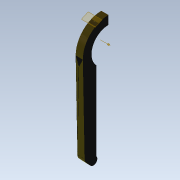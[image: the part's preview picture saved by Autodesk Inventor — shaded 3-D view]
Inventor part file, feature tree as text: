
AUTODESK INVENTOR PART (.ipt)
format: ipt  version: 2021 (Build 250183000, 183)  size: 1,088,512 bytes
history: native  units: mm
features: other x10, sketch x5, extrude x3, hole x2, plane x1, reference x1
ambient origin geometry x8: Origin, YZ Plane, XZ Plane, XY Plane, X Axis, Y Axis, Z Axis, Center Point
bodies: Body1 (feature_tree), Body2 (feature_tree)
feature tree (22):
  other  "Sólido1"
  extrude  "Extrusión1"  Depth=4.0mm
  other  "Superficie reglada1"
  other  "Engrosado1"
  other  "Punto de trabajo1"
  extrude  "Extrusión2"  Depth=34.0mm TaperAngle=0.0deg
  hole  "Agujero1"  [1 undecoded]
  hole  "Agujero2"  [1 undecoded]
  plane  "Plano de trabajo1"
  extrude  "Extrusión3"  [1 undecoded]
  sketch  "Boceto1"  dims[d1=2100.0mm d6=4.0mm]
  other  "Imagen1"
  other  "Sup1"
  other  "Eje de trabajo1"
  sketch  "Boceto2"  dims[d9=3.0mm d10=0.0mm d11=34.0mm d12=0.0mm]
  sketch  "Boceto3"  dims[d13=3.0mm d14=3.0mm]
  sketch  "Boceto4"  dims[d15=0.0mm d16=0.0mm]
  sketch  "Boceto5"  dims[d17=3.4mm d18=6.0mm d19=4.0mm d20=2.0mm d21=90.0deg d22=8.0mm d23=0.0mm d24=3.4mm d25=6.0mm d26=4.0mm d27=2.0mm d28=90.0deg d29=8.0mm d30=0.0mm d32=0.0mm d33=0.0mm]
  reference  "Referencia1"
  parser-record x1  (decoder bookkeeping rows leaked as tree rows — omitted from the tree; the rows remain in map.json)
  other  "ensamble_general.iam"
  other  "platina_2:1"
note: 3 required parameter values undecoded (feature->parameter linkage not recoverable at this tier; creation-order binding heuristic only, values carry confidence <= 0.55)
note: 1 file-system path scrubbed to <path> (originals preserved in map.json)
